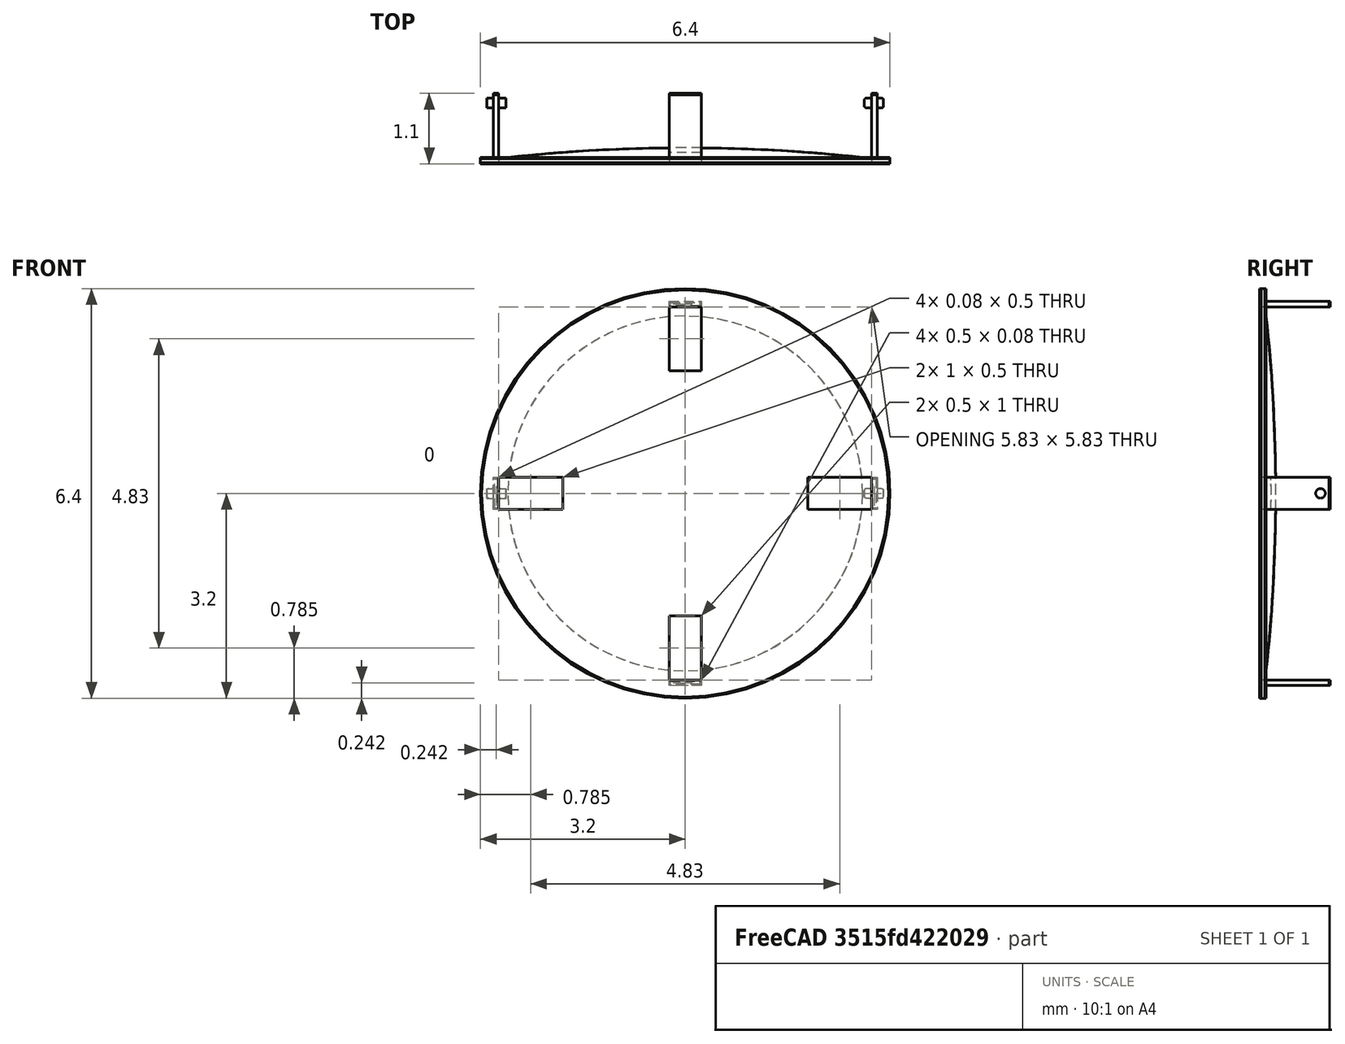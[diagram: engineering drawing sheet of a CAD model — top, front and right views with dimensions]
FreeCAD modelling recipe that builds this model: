
FCSTD DOCUMENT  (FreeCAD 0.16R6712 (Git))
Label: fixanode
License: All rights reserved
LicenseURL: http://en.wikipedia.org/wiki/All_rights_reserved
objects: Sketcher::SketchObject×6, PartDesign::Pad×4, PartDesign::PolarPattern×2, PartDesign::Chamfer×2, PartDesign::Revolution×1, Part::MultiFuse×1, PartDesign::Pocket×1, PartDesign::Fillet×1, Mesh::Feature×1
note: 24 computed .brp shape members not serialized (recipe doc carries the construction recipe); baked Part::Feature solids carry a one-line shape summary decoded from their .brp

FEATURE [Sketcher::SketchObject] Sketch
  Placement = pos=(0,0,0) rot=(1,0,0;1.5708rad)
  sketch-geometry (1):
    g0: Circle CenterX=0 CenterY=0 CenterZ=0 NormalX=0 NormalY=0 NormalZ=1 Radius=3.2
  constraints (2):
    c: Coincident(g0,g-1)
    c: Radius(g0) = 3.2
FEATURE [PartDesign::Pad] Pad
  Length = 0.1
  Length2 = 100
  Midplane = true
  Placement = pos=(0,0,0) rot=(1,0,0;1.5708rad)
  Sketch = -> Sketch
  Type = 0
FEATURE [Sketcher::SketchObject] Sketch001
  Placement = pos=(0,0.05,0) rot=(-1,0,0;1.5708rad)
  Support = -> Pad [Face2]
  sketch-geometry (4):
    g0: LineSegment StartX=-2.91518 StartY=0.25 StartZ=0 EndX=-3 EndY=0.25 EndZ=0
    g1: LineSegment StartX=-3 StartY=0.25 StartZ=0 EndX=-3 EndY=-0.25 EndZ=0
    g2: LineSegment StartX=-3 StartY=-0.25 StartZ=0 EndX=-2.91518 EndY=-0.25 EndZ=0
    g3: LineSegment StartX=-2.91518 StartY=-0.25 StartZ=0 EndX=-2.91518 EndY=0.25 EndZ=0
  constraints (11):
    c: Coincident(g0,g1)
    c: Coincident(g1,g2)
    c: Coincident(g2,g3)
    c: Coincident(g3,g0)
    c: Horizontal(g0)
    c: Horizontal(g2)
    c: Vertical(g1)
    c: Vertical(g3)
    c: Symmetric(g1,g0,g-1)
    c: DistanceX(g-2,g0) = -3
    c: Distance(g0,g2) = 0.5
FEATURE [PartDesign::Pad] Pad001
  Length = 1
  Length2 = 100
  Placement = pos=(0,0,0) rot=(1,0,0;1.5708rad)
  Sketch = -> Sketch001
  Type = 0
FEATURE [PartDesign::PolarPattern] PolarPattern
  Angle = 360
  Axis = -> Sketch001 [N_Axis]
  Occurrences = 4
  Originals = -> [Pad001]
  Placement = pos=(0,0,0) rot=(1,0,0;1.5708rad)
FEATURE [Sketcher::SketchObject] Sketch002
  sketch-geometry (3):
    g0: LineSegment StartX=-3.2 StartY=0 StartZ=0 EndX=0 EndY=0 EndZ=0
    g1: LineSegment StartX=0 StartY=0 StartZ=0 EndX=0 EndY=0.2 EndZ=0
    g2: ArcOfCircle CenterX=0 CenterY=-25.5 CenterZ=0 NormalX=0 NormalY=0 NormalZ=1 Radius=25.7 StartAngle=1.5708 EndAngle=1.69563
  constraints (11):
    c: Coincident(g0,g1)
    c: Horizontal(g0)
    c: Vertical(g1)
    c: PointOnObject(g1,g-2)
    c: PointOnObject(g2,g0)
    c: PointOnObject(g0,g-1)
    c: Coincident(g1,g2)
    c: Coincident(g0,g2)
    c: Perpendicular(g2,g1)
    c: DistanceY(g-1,g1) = 0.2
    c: DistanceX(g-2,g0) = -3.2
FEATURE [PartDesign::Revolution] Revolution
  Angle = 360
  Axis = (0,1,0)
  Base = (0,0,0)
  ReferenceAxis = -> Sketch002 [V_Axis]
  Sketch = -> Sketch002
FEATURE [Part::MultiFuse] Fusion
  Shapes = -> [Revolution,PolarPattern]
FEATURE [Sketcher::SketchObject] Sketch003
  Placement = pos=(0,0.05,0) rot=(0,0.707107,0.707107;3.14159rad)
  Support = -> Fusion [Face3]
  sketch-geometry (4):
    g0: LineSegment StartX=-2.915 StartY=0.249765 StartZ=0 EndX=-1.915 EndY=0.249765 EndZ=0
    g1: LineSegment StartX=-1.915 StartY=0.249765 StartZ=0 EndX=-1.915 EndY=-0.249765 EndZ=0
    g2: LineSegment StartX=-1.915 StartY=-0.249765 StartZ=0 EndX=-2.915 EndY=-0.249765 EndZ=0
    g3: LineSegment StartX=-2.915 StartY=-0.249765 StartZ=0 EndX=-2.915 EndY=0.249765 EndZ=0
  constraints (11):
    c: Coincident(g0,g1)
    c: Coincident(g1,g2)
    c: Coincident(g2,g3)
    c: Coincident(g3,g0)
    c: Horizontal(g0)
    c: Horizontal(g2)
    c: Vertical(g1)
    c: Vertical(g3)
    c: Distance(g-1,g3) = 2.915
    c: Distance(g0,g3) = 1
    c: Symmetric(g1,g0,g-1)
FEATURE [PartDesign::Pocket] Pocket
  Length = 14
  Midplane = true
  Sketch = -> Sketch003
  Type = 0
FEATURE [PartDesign::PolarPattern] PolarPattern001
  Angle = 360
  Axis = -> Sketch003 [N_Axis]
  Occurrences = 4
  Originals = -> [Pocket]
FEATURE [PartDesign::Chamfer] Chamfer
  Base = -> PolarPattern001 [Edge111,Edge108,Edge105,Edge109,Edge39,Edge40,Edge7,Edge3,Edge103,Edge100,Edge97,Edge101,Edge46,Edge50,Edge52,Edge49]
  Size = 0.02
FEATURE [PartDesign::Chamfer] Chamfer001
  Base = -> Chamfer [Edge121,Edge11]
  Size = 0.02
FEATURE [Sketcher::SketchObject] Sketch004
  Placement = pos=(-3,0,0) rot=(0.57735,-0.57735,-0.57735;2.0944rad)
  Support = -> Chamfer001 [Face5]
  sketch-geometry (1):
    g0: Circle CenterX=-0.9 CenterY=0 CenterZ=0 NormalX=0 NormalY=0 NormalZ=1 Radius=0.075
  constraints (3):
    c: PointOnObject(g0,g-1)
    c: Radius(g0) = 0.075
    c: Distance(g-1,g0) = 0.9
FEATURE [PartDesign::Pad] Pad002
  Length = 0.1
  Length2 = 0.2
  Sketch = -> Sketch004
  Type = 4
FEATURE [Sketcher::SketchObject] Sketch005
  Placement = pos=(3,0,0) rot=(0.57735,0.57735,0.57735;2.0944rad)
  Support = -> Pad002 [Face37]
  sketch-geometry (1):
    g0: Circle CenterX=0.9 CenterY=0 CenterZ=0 NormalX=0 NormalY=0 NormalZ=1 Radius=0.075
  constraints (3):
    c: Radius(g0) = 0.075
    c: PointOnObject(g0,g-1)
    c: Distance(g-1,g0) = 0.9
FEATURE [PartDesign::Pad] Pad003
  Length = 0.1
  Length2 = 0.2
  Sketch = -> Sketch005
  Type = 4
FEATURE [PartDesign::Fillet] Fillet
  Base = -> Pad003 [Edge124,Edge162,Edge118,Edge154,Edge48,Edge126,Edge3,Edge1]
  Radius = 0.03
FEATURE [Mesh::Feature] Mesh  label="Fillet (Meshed)"
  Placement = pos=(0,-1,0) rot=(0,0,1;0rad)
